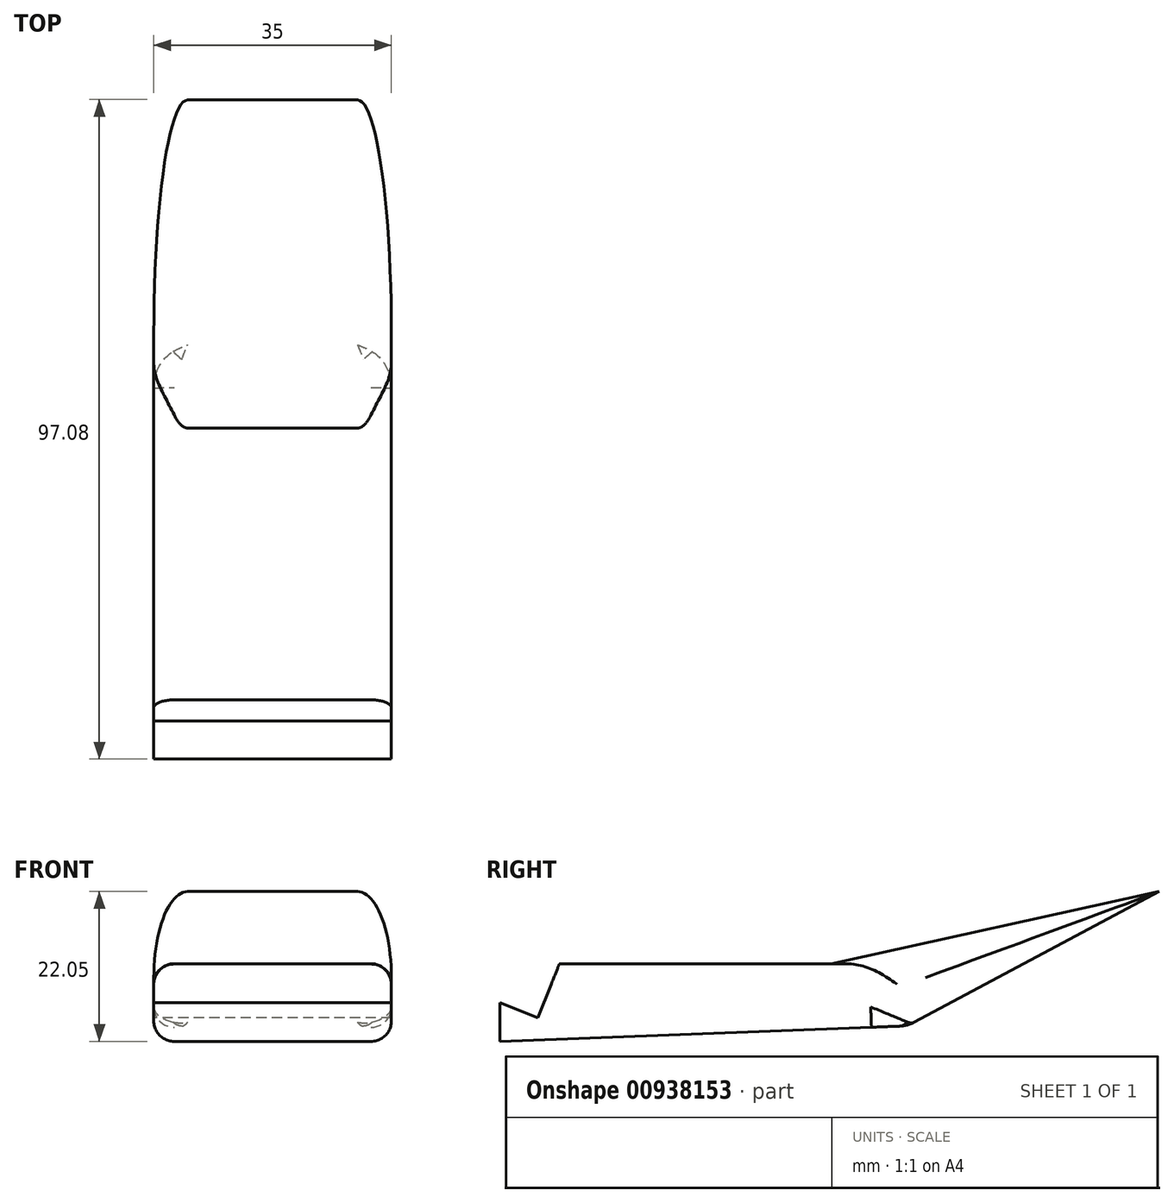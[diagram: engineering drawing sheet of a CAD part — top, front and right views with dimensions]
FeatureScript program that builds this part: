
annotation { "Feature Type Name" : "Feature", "Feature Type Description" : "" }
export const myFeature = defineFeature(function(context is Context, id is Id, definition is map)
    precondition{}
    {
        {
            var Q0;
            Q0=qCreatedBy(makeId("Right.planeOp"),FACE);
            var sketch = newSketch(context, id + "F0", { "sketchPlane" : qUnion([Q0])});
            skLineSegment(sketch, "E0.MirrorCS", {"start": v(-59.88, 30.77) * mm, "end": v(-59.88, 36.47) * mm});
            skLineSegment(sketch, "E1", {"start": v(-59.88, 36.47) * mm, "end": v(-54.3, 34.25) * mm});
            skLineSegment(sketch, "E2", {"start": v(-54.3, 34.25) * mm, "end": v(-51.16, 42.15) * mm});
            skLineSegment(sketch, "E3", {"start": v(-59.88, 30.77) * mm, "end": v(0.08, 33.04) * mm});
            skLineSegment(sketch, "E4", {"start": v(-51.16, 42.15) * mm, "end": v(-11.16, 42.2) * mm});
            skLineSegment(sketch, "E5", {"start": v(-11.16, 42.2) * mm, "end": v(37.2, 52.82) * mm});
            skLineSegment(sketch, "E6", {"start": v(37.2, 52.82) * mm, "end": v(0.08, 33.04) * mm});
            skSolve(sketch);
        }
        {
            var Q0;
            Q0=qSketchRegion(id+"F0",true);
            extrude(context, id + "F1", {"entities" : qUnion([Q0]), "depth" : 35 * mm, "offsetDistance" : 25 * mm});
        }
        {
            var Q0;
            Q0=makeQuery(id+"F1.opExtrude","CAP_EDGE",EDGE,{"disambiguationData":[OSD([sQuery(id+"F0.wireOp",EDGE,"E4")])],"isStart":true});
            var Q1;
            Q1=makeQuery(id+"F1.opExtrude","CAP_EDGE",EDGE,{"disambiguationData":[OSD([sQuery(id+"F0.wireOp",EDGE,"a55549ca-b96a-4656-8882-2c1fbc8c65ad.MirrorCS")])],"isStart":false});
            var Q2;
            Q2=makeQuery(id+"F1.opExtrude","CAP_EDGE",EDGE,{"disambiguationData":[OSD([sQuery(id+"F0.wireOp",EDGE,"a55549ca-b96a-4656-8882-2c1fbc8c65ad.MirrorCS")])],"isStart":true});
            var Q3;
            Q3=makeQuery(id+"F1.opExtrude","CAP_EDGE",EDGE,{"disambiguationData":[OSD([sQuery(id+"F0.wireOp",EDGE,"E3")])],"isStart":true});
            var Q4;
            Q4=makeQuery(id+"F1.opExtrude","CAP_EDGE",EDGE,{"disambiguationData":[OSD([sQuery(id+"F0.wireOp",EDGE,"E4")])],"isStart":false});
            var Q5;
            Q5=makeQuery(id+"F1.opExtrude","CAP_EDGE",EDGE,{"disambiguationData":[OSD([sQuery(id+"F0.wireOp",EDGE,"E3")])],"isStart":false});
            fillet(context, id + "F2", {"entities" : qUnion([Q0, Q1, Q2, Q3, Q4, Q5]), "radius" : 3 * mm, "tangentPropagation" : true, "allowEdgeOverflow" : false});
        }
        {
            var Q0;
            Q0=makeQuery(id+"F1.opExtrude","CAP_EDGE",EDGE,{"disambiguationData":[OSD([sQuery(id+"F0.wireOp",EDGE,"E5")])],"isStart":false});
            var Q1;
            Q1=makeQuery(id+"F1.opExtrude","CAP_EDGE",EDGE,{"disambiguationData":[OSD([sQuery(id+"F0.wireOp",EDGE,"E6")])],"isStart":false});
            var Q2;
            Q2=makeQuery(id+"F1.opExtrude","CAP_EDGE",EDGE,{"disambiguationData":[OSD([sQuery(id+"F0.wireOp",EDGE,"E5")])],"isStart":true});
            fillet(context, id + "F3", {"entities" : qUnion([Q0, Q1, Q2]), "radius" : 5 * mm, "tangentPropagation" : true, "allowEdgeOverflow" : false});
        }
    });
